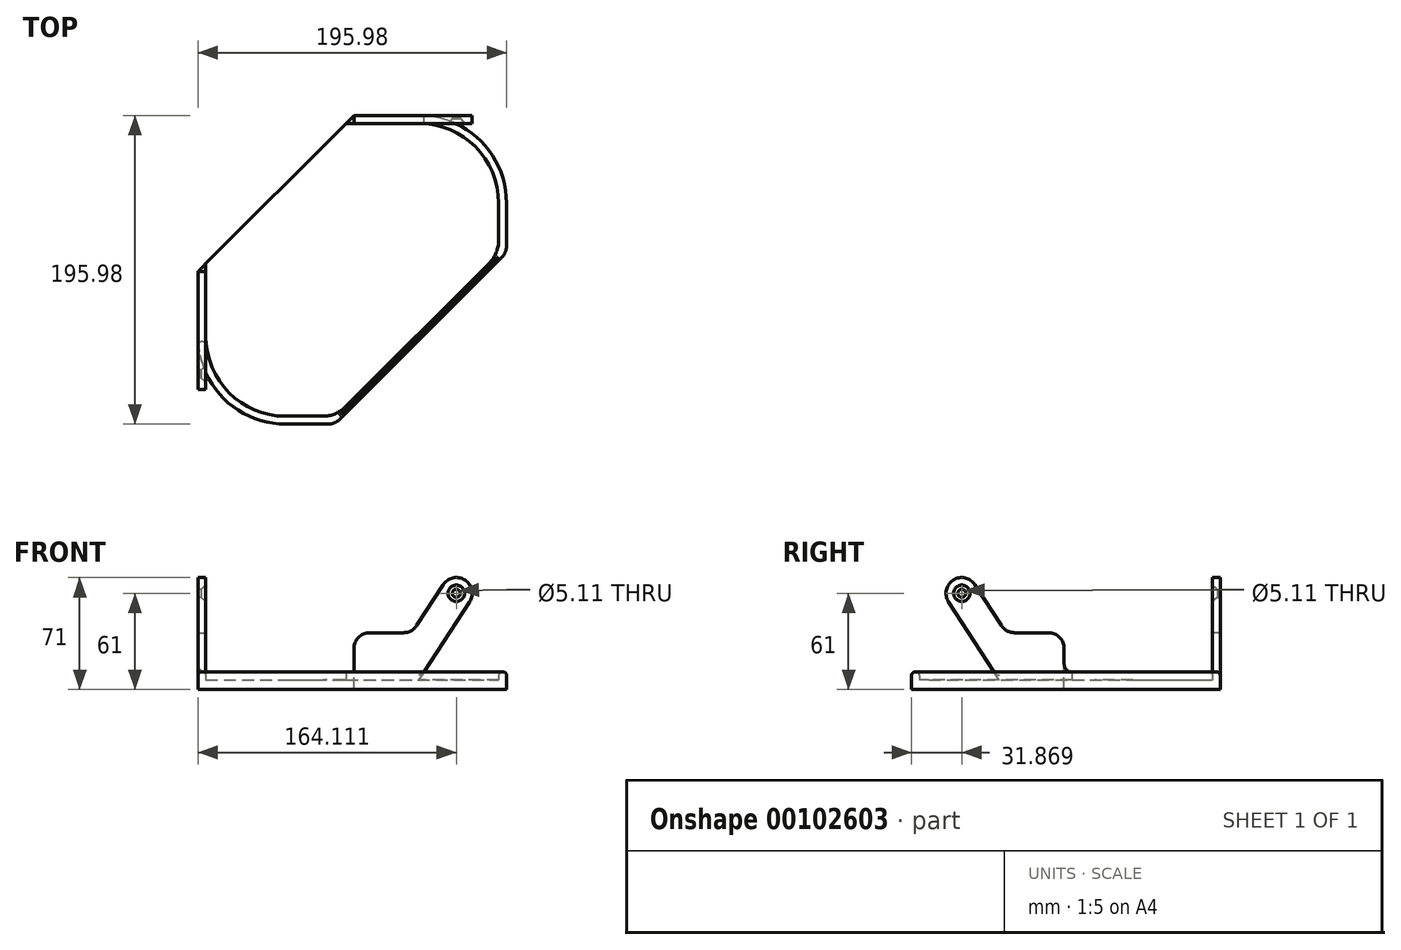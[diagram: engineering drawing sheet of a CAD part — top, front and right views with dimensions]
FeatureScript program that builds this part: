
annotation { "Feature Type Name" : "Feature", "Feature Type Description" : "" }
export const myFeature = defineFeature(function(context is Context, id is Id, definition is map)
    precondition{}
    {
        {
            var Q0;
            Q0=qCreatedBy(makeId("Top.planeOp"),FACE);
            var sketch = newSketch(context, id + "F0", { "sketchPlane" : qUnion([Q0])});
            skLineSegment(sketch, "E0.bottom", {"start": v(0, 0) * mm, "end": v(140.4, 0) * mm});
            skLineSegment(sketch, "E0.top", {"start": v(55.58, -195.98) * mm, "end": v(82.83, -195.98) * mm});
            skLineSegment(sketch, "E0.left", {"start": v(0, 0) * mm, "end": v(0, -140.4) * mm});
            skLineSegment(sketch, "E0.right", {"start": v(195.98, -55.58) * mm, "end": v(195.98, -82.83) * mm});
            skPoint(sketch, "E1.visualSharp", {"position": v(0, -195.98) * mm});
            skArc(sketch, "E1.filletArc", {"start": v(0, -140.4) * mm, "mid": v(16.28, -179.7) * mm, "end": v(55.58, -195.98) * mm});
            skPoint(sketch, "E2.visualSharp", {"position": v(195.98, 0) * mm});
            skArc(sketch, "E2.filletArc", {"start": v(195.98, -55.58) * mm, "mid": v(179.7, -16.28) * mm, "end": v(140.4, 0) * mm});
            skPoint(sketch, "E3.visualSharp", {"position": v(195.98, -195.98) * mm});
            skLineSegment(sketch, "E4.0", {"start": v(5, -5) * mm, "end": v(5, -140.4) * mm});
            skLineSegment(sketch, "E4.1", {"start": v(5, -5) * mm, "end": v(140.4, -5) * mm});
            skLineSegment(sketch, "E4.2", {"start": v(55.58, -190.98) * mm, "end": v(83.59, -190.98) * mm});
            skLineSegment(sketch, "E4.4", {"start": v(190.98, -55.58) * mm, "end": v(190.98, -79.45) * mm});
            skArc(sketch, "E4.5", {"start": v(5, -140.4) * mm, "mid": v(19.81, -176.17) * mm, "end": v(55.58, -190.98) * mm});
            skArc(sketch, "E4.6", {"start": v(190.98, -55.58) * mm, "mid": v(176.17, -19.81) * mm, "end": v(140.4, -5) * mm});
            skLineSegment(sketch, "E5", {"start": v(85.62, -110.37) * mm, "end": v(110.37, -85.62) * mm, "construction": true});
            skArc(sketch, "E6.0.startCap", {"start": v(126.28, -151.03) * mm, "mid": v(44.96, -151.03) * mm, "end": v(44.96, -69.7) * mm, "construction": true});
            skArc(sketch, "E6.0.endCap", {"start": v(69.7, -44.96) * mm, "mid": v(151.03, -44.96) * mm, "end": v(151.03, -126.28) * mm, "construction": true});
            skLineSegment(sketch, "E6.0.left", {"start": v(44.96, -69.7) * mm, "end": v(69.7, -44.96) * mm, "construction": true});
            skLineSegment(sketch, "E6.0.right", {"start": v(126.28, -151.03) * mm, "end": v(151.03, -126.28) * mm, "construction": true});
            skLineSegment(sketch, "E7", {"start": v(98, -98) * mm, "end": v(5, -5) * mm, "construction": true});
            skLineSegment(sketch, "E8", {"start": v(0, -99.11) * mm, "end": v(99.11, 0) * mm});
            skLineSegment(sketch, "E9", {"start": v(90.66, -188.06) * mm, "end": v(185.13, -93.59) * mm});
            skLineSegment(sketch, "E10", {"start": v(89.9, -193.06) * mm, "end": v(193.06, -89.9) * mm});
            skPoint(sketch, "E11.visualSharp", {"position": v(87.73, -190.98) * mm});
            skArc(sketch, "E11.filletArc", {"start": v(83.59, -190.98) * mm, "mid": v(87.42, -190.22) * mm, "end": v(90.66, -188.06) * mm});
            skPoint(sketch, "E12.visualSharp", {"position": v(86.97, -195.98) * mm});
            skArc(sketch, "E12.filletArc", {"start": v(82.83, -195.98) * mm, "mid": v(86.66, -195.22) * mm, "end": v(89.9, -193.06) * mm});
            skPoint(sketch, "E13.visualSharp", {"position": v(195.98, -86.97) * mm});
            skArc(sketch, "E13.filletArc", {"start": v(193.06, -89.9) * mm, "mid": v(195.22, -86.66) * mm, "end": v(195.98, -82.83) * mm});
            skPoint(sketch, "E14.visualSharp", {"position": v(190.98, -87.73) * mm});
            skArc(sketch, "E14.filletArc", {"start": v(185.13, -93.59) * mm, "mid": v(189.46, -87.1) * mm, "end": v(190.98, -79.45) * mm});
            skSolve(sketch);
        }
        {
            var Q0;
            {var subQ0=sQuery(id+"F0.wireOp",EDGE,"E0.top");Q0=makeQuery(id+"F0.imprint","IMPRINT",FACE,{"disambiguationData":[TD([[makeQuery(id+"F0.imprint","IMPRINT",EDGE,{"derivedFrom":subQ0}),1.0]])]});}
            var Q1;
            {var subQ0=sQuery(id+"F0.wireOp",EDGE,"E0.right");Q1=makeQuery(id+"F0.imprint","IMPRINT",FACE,{"disambiguationData":[TD([[makeQuery(id+"F0.imprint","IMPRINT",EDGE,{"derivedFrom":subQ0}),-1.0]])]});}
            var Q2;
            {var subQ0=sQuery(id+"F0.wireOp",EDGE,"E4.2");Q2=makeQuery(id+"F0.imprint","IMPRINT",FACE,{"disambiguationData":[TD([[makeQuery(id+"F0.imprint","IMPRINT",EDGE,{"derivedFrom":subQ0}),1.0]])]});}
            var Q3;
            {var subQ5=sQuery(id+"F0.wireOp",EDGE,"E4.2");Q3=makeQuery(id+"F0.imprint","IMPRINT",FACE,{"disambiguationData":[TD([[makeQuery(id+"F0.imprint","IMPRINT",EDGE,{"derivedFrom":subQ5}),-1.0]])]});}
            var Q4;
            {var subQ13=sQuery(id+"F0.wireOp",EDGE,"E9");Q4=makeQuery(id+"F0.imprint","IMPRINT",FACE,{"disambiguationData":[TD([[makeQuery(id+"F0.imprint","IMPRINT",EDGE,{"derivedFrom":subQ13}),1.0]])]});}
            extrude(context, id + "F1", {"entities" : qUnion([Q0, Q1, Q2, Q3, Q4]), "oppositeDirection" : true, "depth" : 6 * mm});
        }
        {
            var Q0;
            Q0=makeQuery(id+"F0.imprint","IMPRINT",FACE,{"disambiguationData":[TD([[makeQuery(id+"F0.imprint","IMPRINT",EDGE,{"derivedFrom":sQuery(id+"F0.wireOp",EDGE,"E0.top")}),1.0]])]});
            extrude(context, id + "F2", {"entities" : qUnion([Q0]), "operationType" : NewBodyOperationType.ADD, "depth" : 5 * mm});
        }
        {
            var Q0;
            Q0=makeQuery(id+"F2.opExtrude","SWEPT_FACE",FACE,{"disambiguationData":[OSD([sQuery(id+"F0.wireOp",EDGE,"E4.0")])]});
            var sketch = newSketch(context, id + "F3", { "sketchPlane" : qUnion([Q0])});
            skLineSegment(sketch, "E15", {"start": v(-140.4, 0) * mm, "end": v(-172.5, 49.56) * mm});
            skLineSegment(sketch, "E16", {"start": v(-99.11, 30) * mm, "end": v(-99.11, 0) * mm});
            skArc(sketch, "E17.filletArc", {"start": v(-164.11, 65) * mm, "mid": v(-172.9, 59.78) * mm, "end": v(-172.5, 49.56) * mm});
            skLineSegment(sketch, "E18", {"start": v(-99.11, 0) * mm, "end": v(-140.4, 0) * mm});
            skArc(sketch, "E19", {"start": v(-155.72, 60.44) * mm, "mid": v(-159.33, 63.79) * mm, "end": v(-164.11, 65) * mm});
            skLineSegment(sketch, "E20", {"start": v(-155.72, 60.44) * mm, "end": v(-138.96, 34.56) * mm});
            skLineSegment(sketch, "E21", {"start": v(-130.57, 30) * mm, "end": v(-99.11, 30) * mm});
            skPoint(sketch, "E22.visualSharp", {"position": v(-136, 30) * mm});
            skArc(sketch, "E22.filletArc", {"start": v(-138.96, 34.56) * mm, "mid": v(-135.35, 31.21) * mm, "end": v(-130.57, 30) * mm});
            skSolve(sketch);
        }
        {
            var Q0;
            Q0=qSketchRegion(id+"F3",true);
            var Q1;
            {var subQ0=sQuery(id+"F0.wireOp",EDGE,"E0.left");Q1=makeQuery(id+"F2.boolean.opBoolean","MERGE",FACE,{"derivedFrom":[makeQuery(id+"F1.opExtrude","SWEPT_FACE",FACE,{"disambiguationData":[OSD([subQ0])]}),makeQuery(id+"F2.opExtrude","SWEPT_FACE",FACE,{"disambiguationData":[OSD([subQ0])]})]});}
            extrude(context, id + "F4", {"entities" : qUnion([Q0]), "operationType" : NewBodyOperationType.ADD, "endBound" : BoundingType.UP_TO_SURFACE, "oppositeDirection" : true, "endBoundEntityFace" : qUnion([Q1]), "depth" : 25 * mm});
        }
        {
            var Q0;
            Q0=sQuery(id+"F3.wireOp",VERTEX,"E17.filletArc.center");
            var Q1;
            Q1=makeQuery(id+"F1.opExtrude","SWEPT_BODY",BODY,{"disambiguationData":[OSD([sQuery(id+"F0.wireOp",EDGE,"E0.bottom"),sQuery(id+"F0.wireOp",EDGE,"E0.top"),sQuery(id+"F0.wireOp",EDGE,"E0.left"),sQuery(id+"F0.wireOp",EDGE,"E0.right"),sQuery(id+"F0.wireOp",EDGE,"E1.filletArc"),sQuery(id+"F0.wireOp",EDGE,"E2.filletArc"),sQuery(id+"F0.wireOp",EDGE,"E3.filletArc"),sQuery(id+"F0.wireOp",EDGE,"E4.0"),sQuery(id+"F0.wireOp",EDGE,"E4.1"),sQuery(id+"F0.wireOp",EDGE,"07iE15DX-D2Cc-ar4g-h2nO-7O1ppVkISamw")])]});
            hole(context, id + "F5", {"style" : HoleStyle.C_SINK, "endStyle" : HoleEndStyle.THROUGH, "standardTappedOrClearance" : lookupTablePath({ "standard" : "ANSI", "fit" : "Normal (ASME)", "size" : "#10", "type" : "Clearance" }), "standardBlindInLast" : lookupTablePath({ "fit" : "Free", "standard" : "ANSI", "size" : "#10", "type" : "Clearance" }), "holeDiameter" : 5.1 * mm, "cSinkDiameter" : 10.44 * mm, "cSinkAngle" : 82 * degree, "tappedDepth" : 12 * mm, "tapClearance" : 3, "locations" : qUnion([Q0]), "scope" : qUnion([Q1]), "startStyle" : HoleStartStyle.PART});
        }
        {
            var Q0;
            Q0=qCreatedBy(makeId("Front.planeOp"),FACE);
            var Q1;
            Q1=qCreatedBy(makeId("Right.planeOp"),FACE);
            cPlane(context, id + "F6", {"entities" : qUnion([Q0, Q1]), "cplaneType" : CPlaneType.MID_PLANE, "offset" : 25 * mm, "width" : 150 * mm, "height" : 150 * mm});
        }
        {
            var Q0;
            Q0=makeQuery(id+"F4.opExtrude","SWEPT_EDGE",EDGE,{"disambiguationData":[OSD([sQuery(id+"F3.wireOp",EDGE,"E16"),sQuery(id+"F3.wireOp",EDGE,"E21")])]});
            fillet(context, id + "F7", {"entities" : qUnion([Q0]), "radius" : 10 * mm, "tangentPropagation" : true, "allowEdgeOverflow" : false});
        }
        {
            var Q0;
            Q0=makeQuery(id+"F1.opExtrude","SWEPT_BODY",BODY,{"disambiguationData":[OSD([sQuery(id+"F0.wireOp",EDGE,"E0.bottom"),sQuery(id+"F0.wireOp",EDGE,"E0.top"),sQuery(id+"F0.wireOp",EDGE,"E0.left"),sQuery(id+"F0.wireOp",EDGE,"E0.right"),sQuery(id+"F0.wireOp",EDGE,"E1.filletArc"),sQuery(id+"F0.wireOp",EDGE,"E2.filletArc"),sQuery(id+"F0.wireOp",EDGE,"E3.filletArc"),sQuery(id+"F0.wireOp",EDGE,"E4.0"),sQuery(id+"F0.wireOp",EDGE,"E4.1"),sQuery(id+"F0.wireOp",EDGE,"07iE15DX-D2Cc-ar4g-h2nO-7O1ppVkISamw")])]});
            var Q1;
            Q1=qCreatedBy(id+"F6.planeOp",FACE);
            mirror(context, id + "F8", {"operationType" : NewBodyOperationType.ADD, "entities" : qUnion([Q0]), "mirrorPlane" : qUnion([Q1])});
        }
        {
            var Q0;
            Q0=makeQuery(id+"F2.opExtrude","CAP_EDGE",EDGE,{"disambiguationData":[OSD([sQuery(id+"F0.wireOp",EDGE,"E4.5")])],"isStart":true});
            var Q1;
            Q1=makeQuery(id+"F2.opExtrude","CAP_EDGE",EDGE,{"disambiguationData":[OSD([sQuery(id+"F0.wireOp",EDGE,"E4.4")])],"isStart":false});
            var Q2;
            Q2=makeQuery(id+"F2.opExtrude","CAP_EDGE",EDGE,{"disambiguationData":[OSD([sQuery(id+"F0.wireOp",EDGE,"E3.filletArc")])],"isStart":false});
            var Q3;
            {var subQ0=sQuery(id+"F0.wireOp",EDGE,"E4.1");var subQ1=sQuery(id+"F0.wireOp",EDGE,"E4.0");Q3=makeQuery(id+"F2.boolean.opBoolean","MERGE",EDGE,{"derivedFrom":[makeQuery(id+"F1.opExtrude","SWEPT_EDGE",EDGE,{"disambiguationData":[OSD([subQ1,subQ0])]}),makeQuery(id+"F2.opExtrude","SWEPT_EDGE",EDGE,{"disambiguationData":[OSD([subQ1,subQ0])]})]});}
            var Q4;
            Q4=makeQuery(id+"F2.opExtrude","CAP_EDGE",EDGE,{"disambiguationData":[OSD([sQuery(id+"F0.wireOp",EDGE,"E1.filletArc")])],"isStart":false});
            fillet(context, id + "F9", {"entities" : qUnion([Q0, Q1, Q2, Q3, Q4]), "radius" : 2 * mm, "tangentPropagation" : true, "allowEdgeOverflow" : false});
        }
        {
            var Q0;
            Q0=makeQuery(id+"F4.boolean.opBoolean","INTERSECT",EDGE,{"derivedFrom":[makeQuery(id+"F2.opExtrude","CAP_FACE",FACE,{"disambiguationData":[OSD([sQuery(id+"F0.wireOp",EDGE,"E0.bottom"),sQuery(id+"F0.wireOp",EDGE,"E0.top"),sQuery(id+"F0.wireOp",EDGE,"E0.left"),sQuery(id+"F0.wireOp",EDGE,"E0.right"),sQuery(id+"F0.wireOp",EDGE,"E1.filletArc"),sQuery(id+"F0.wireOp",EDGE,"E2.filletArc"),sQuery(id+"F0.wireOp",EDGE,"E4.0"),sQuery(id+"F0.wireOp",EDGE,"E4.1"),sQuery(id+"F0.wireOp",EDGE,"E4.2"),sQuery(id+"F0.wireOp",EDGE,"E4.4"),sQuery(id+"F0.wireOp",EDGE,"E4.5"),sQuery(id+"F0.wireOp",EDGE,"E4.6"),sQuery(id+"F0.wireOp",EDGE,"E8"),sQuery(id+"F0.wireOp",EDGE,"E9"),sQuery(id+"F0.wireOp",EDGE,"E10"),sQuery(id+"F0.wireOp",EDGE,"E11.filletArc"),sQuery(id+"F0.wireOp",EDGE,"E12.filletArc"),sQuery(id+"F0.wireOp",EDGE,"E13.filletArc"),sQuery(id+"F0.wireOp",EDGE,"E14.filletArc")])],"isStart":false}),makeQuery(id+"F4.opExtrude","SWEPT_FACE",FACE,{"disambiguationData":[OSD([sQuery(id+"F3.wireOp",EDGE,"E16")])]})]});
            var Q1;
            Q1=makeQuery(id+"F8.opPattern","COPY",EDGE,{"derivedFrom":makeQuery(id+"F4.boolean.opBoolean","INTERSECT",EDGE,{"derivedFrom":[makeQuery(id+"F2.opExtrude","CAP_FACE",FACE,{"disambiguationData":[OSD([sQuery(id+"F0.wireOp",EDGE,"E0.bottom"),sQuery(id+"F0.wireOp",EDGE,"E0.top"),sQuery(id+"F0.wireOp",EDGE,"E0.left"),sQuery(id+"F0.wireOp",EDGE,"E0.right"),sQuery(id+"F0.wireOp",EDGE,"E1.filletArc"),sQuery(id+"F0.wireOp",EDGE,"E2.filletArc"),sQuery(id+"F0.wireOp",EDGE,"E4.0"),sQuery(id+"F0.wireOp",EDGE,"E4.1"),sQuery(id+"F0.wireOp",EDGE,"E4.2"),sQuery(id+"F0.wireOp",EDGE,"E4.4"),sQuery(id+"F0.wireOp",EDGE,"E4.5"),sQuery(id+"F0.wireOp",EDGE,"E4.6"),sQuery(id+"F0.wireOp",EDGE,"E8"),sQuery(id+"F0.wireOp",EDGE,"E9"),sQuery(id+"F0.wireOp",EDGE,"E10"),sQuery(id+"F0.wireOp",EDGE,"E11.filletArc"),sQuery(id+"F0.wireOp",EDGE,"E12.filletArc"),sQuery(id+"F0.wireOp",EDGE,"E13.filletArc"),sQuery(id+"F0.wireOp",EDGE,"E14.filletArc")])],"isStart":false}),makeQuery(id+"F4.opExtrude","SWEPT_FACE",FACE,{"disambiguationData":[OSD([sQuery(id+"F3.wireOp",EDGE,"E16")])]})]}),"instanceName":"1"});
            fillet(context, id + "F10", {"entities" : qUnion([Q0, Q1]), "radius" : 5 * mm, "tangentPropagation" : true, "allowEdgeOverflow" : false});
        }
    });
